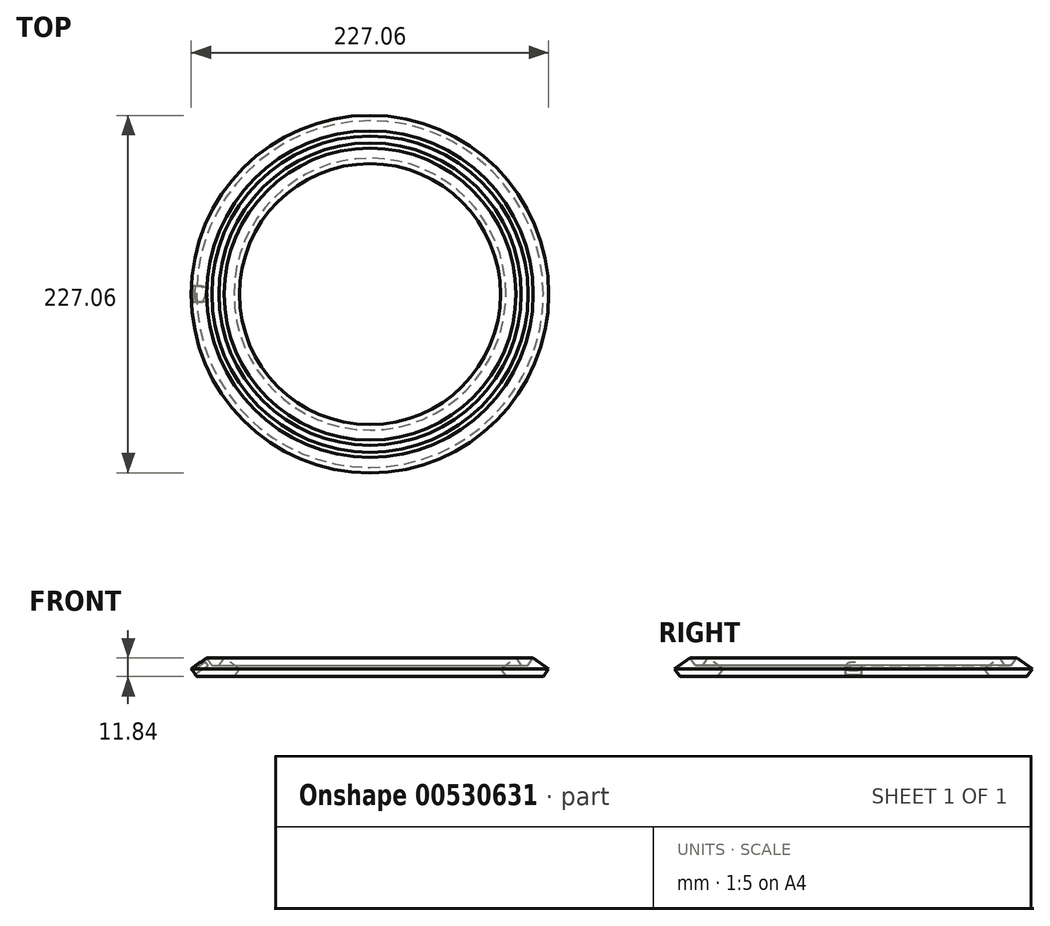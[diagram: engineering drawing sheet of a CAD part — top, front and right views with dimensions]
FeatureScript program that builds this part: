
annotation { "Feature Type Name" : "Feature", "Feature Type Description" : "" }
export const myFeature = defineFeature(function(context is Context, id is Id, definition is map)
    precondition{}
    {
        {
            var Q0;
            Q0=qCreatedBy(makeId("Front.planeOp"),FACE);
            var sketch = newSketch(context, id + "F0", { "sketchPlane" : qUnion([Q0])});
            skLineSegment(sketch, "E0", {"start": v(-110.1, 0) * mm, "end": v(-113.53, 4.92) * mm});
            skLineSegment(sketch, "E1", {"start": v(-113.53, 4.92) * mm, "end": v(-103.68, 11.78) * mm});
            skLineSegment(sketch, "E2", {"start": v(-103.68, 11.78) * mm, "end": v(-100.43, 7.11) * mm});
            skLineSegment(sketch, "E3", {"start": v(-100.43, 7.11) * mm, "end": v(-96.01, 7.11) * mm});
            skLineSegment(sketch, "E4", {"start": v(-96.01, 7.11) * mm, "end": v(-92.67, 11.84) * mm});
            skLineSegment(sketch, "E5", {"start": v(-92.67, 11.84) * mm, "end": v(-82.88, 4.9) * mm});
            skLineSegment(sketch, "E6", {"start": v(-82.88, 4.9) * mm, "end": v(-86.35, 0) * mm});
            skLineSegment(sketch, "E7", {"start": v(-86.35, 0) * mm, "end": v(-110.1, 0) * mm});
            skLineSegment(sketch, "E8", {"start": v(-112.67, 3.7) * mm, "end": v(-104.47, 9.41) * mm});
            skLineSegment(sketch, "E9", {"start": v(-104.47, 9.41) * mm, "end": v(-102.75, 6.95) * mm});
            skLineSegment(sketch, "E10", {"start": v(-102.75, 6.95) * mm, "end": v(-110.96, 1.23) * mm});
            skLineSegment(sketch, "E11", {"start": v(-83.74, 3.67) * mm, "end": v(-91.9, 9.46) * mm});
            skLineSegment(sketch, "E12", {"start": v(-91.9, 9.46) * mm, "end": v(-93.64, 7) * mm});
            skLineSegment(sketch, "E13", {"start": v(-93.64, 7) * mm, "end": v(-85.48, 1.22) * mm});
            skLineSegment(sketch, "E14", {"start": v(-103.61, 8.18) * mm, "end": v(-101.97, 9.32) * mm});
            skLineSegment(sketch, "E15", {"start": v(-92.77, 8.23) * mm, "end": v(-94.4, 9.39) * mm});
            skLineSegment(sketch, "E16", {"start": v(-103.76, 8.4) * mm, "end": v(-102.12, 9.54) * mm});
            skLineSegment(sketch, "E17", {"start": v(-103.46, 7.96) * mm, "end": v(-101.82, 9.1) * mm});
            skLineSegment(sketch, "E18", {"start": v(-92.91, 8.03) * mm, "end": v(-94.55, 9.18) * mm});
            skLineSegment(sketch, "E19", {"start": v(-94.26, 9.6) * mm, "end": v(-92.62, 8.44) * mm});
            skLineSegment(sketch, "E20", {"start": v(-108.57, 6.55) * mm, "end": v(-106.85, 4.09) * mm});
            skLineSegment(sketch, "E21", {"start": v(-87.82, 6.56) * mm, "end": v(-89.56, 4.12) * mm});
            skLineSegment(sketch, "E22", {"start": v(0, 0) * mm, "end": v(0, 20.5) * mm});
            skSolve(sketch);
        }
        {
            var Q0;
            {var subQ1=sQuery(id+"F0.wireOp",EDGE,"E1");Q0=makeQuery(id+"F0.imprint","IMPRINT",FACE,{"disambiguationData":[TD([[makeQuery(id+"F0.imprint","IMPRINT",EDGE,{"derivedFrom":subQ1}),-1.0]])]});}
            var Q1;
            {var subQ5=sQuery(id+"F0.wireOp",EDGE,"E20");Q1=makeQuery(id+"F0.imprint","IMPRINT",FACE,{"disambiguationData":[TD([[makeQuery(id+"F0.imprint","IMPRINT",EDGE,{"derivedFrom":subQ5}),-1.0]])]});}
            var Q2;
            {var subQ4=sQuery(id+"F0.wireOp",EDGE,"E5");Q2=makeQuery(id+"F0.imprint","IMPRINT",FACE,{"disambiguationData":[TD([[makeQuery(id+"F0.imprint","IMPRINT",EDGE,{"derivedFrom":subQ4}),-1.0]])]});}
            var Q3;
            {var subQ11=sQuery(id+"F0.wireOp",EDGE,"E3");Q3=makeQuery(id+"F0.imprint","IMPRINT",FACE,{"disambiguationData":[TD([[makeQuery(id+"F0.imprint","IMPRINT",EDGE,{"derivedFrom":subQ11}),-1.0]])]});}
            var Q4;
            {var subQ0=sQuery(id+"F0.wireOp",EDGE,"E14");Q4=makeQuery(id+"F0.imprint","IMPRINT",FACE,{"disambiguationData":[TD([[makeQuery(id+"F0.imprint","IMPRINT",EDGE,{"derivedFrom":subQ0}),1.0]])]});}
            var Q5;
            {var subQ0=sQuery(id+"F0.wireOp",EDGE,"E14");Q5=makeQuery(id+"F0.imprint","IMPRINT",FACE,{"disambiguationData":[TD([[makeQuery(id+"F0.imprint","IMPRINT",EDGE,{"derivedFrom":subQ0}),-1.0]])]});}
            var Q6;
            {var subQ0=sQuery(id+"F0.wireOp",EDGE,"E15");Q6=makeQuery(id+"F0.imprint","IMPRINT",FACE,{"disambiguationData":[TD([[makeQuery(id+"F0.imprint","IMPRINT",EDGE,{"derivedFrom":subQ0}),1.0]])]});}
            var Q7;
            {var subQ0=sQuery(id+"F0.wireOp",EDGE,"E15");Q7=makeQuery(id+"F0.imprint","IMPRINT",FACE,{"disambiguationData":[TD([[makeQuery(id+"F0.imprint","IMPRINT",EDGE,{"derivedFrom":subQ0}),-1.0]])]});}
            var Q8;
            {var subQ5=sQuery(id+"F0.wireOp",EDGE,"E21");Q8=makeQuery(id+"F0.imprint","IMPRINT",FACE,{"disambiguationData":[TD([[makeQuery(id+"F0.imprint","IMPRINT",EDGE,{"derivedFrom":subQ5}),1.0]])]});}
            var Q9;
            {var subQ6=sQuery(id+"F0.wireOp",EDGE,"E20");Q9=makeQuery(id+"F0.imprint","IMPRINT",FACE,{"disambiguationData":[TD([[makeQuery(id+"F0.imprint","IMPRINT",EDGE,{"derivedFrom":subQ6}),1.0]])]});}
            var Q10;
            {var subQ3=sQuery(id+"F0.wireOp",EDGE,"E21");Q10=makeQuery(id+"F0.imprint","IMPRINT",FACE,{"disambiguationData":[TD([[makeQuery(id+"F0.imprint","IMPRINT",EDGE,{"derivedFrom":subQ3}),-1.0]])]});}
            var Q11;
            Q11=sQuery(id+"F0.wireOp",EDGE,"E22");
            revolve(context, id + "F1", {"entities" : qUnion([Q0, Q1, Q2, Q3, Q4, Q5, Q6, Q7, Q8, Q9, Q10]), "axis" : qUnion([Q11]), "revolveType" : RevolveType.FULL});
        }
        {
            var Q0;
            {var subQ5=sQuery(id+"F0.wireOp",EDGE,"E20");Q0=makeQuery(id+"F0.imprint","IMPRINT",FACE,{"disambiguationData":[TD([[makeQuery(id+"F0.imprint","IMPRINT",EDGE,{"derivedFrom":subQ5}),-1.0]])]});}
            extrude(context, id + "F2", {"entities" : qUnion([Q0]), "operationType" : NewBodyOperationType.REMOVE, "depth" : 5 * mm, "offsetDistance" : 25 * mm, "hasSecondDirection" : true, "secondDirectionOppositeDirection" : true, "secondDirectionDepth" : 5 * mm});
        }
        {
            var Q0;
            {var subQ6=sQuery(id+"F0.wireOp",EDGE,"E20");Q0=makeQuery(id+"F0.imprint","IMPRINT",FACE,{"disambiguationData":[TD([[makeQuery(id+"F0.imprint","IMPRINT",EDGE,{"derivedFrom":subQ6}),1.0]])]});}
            var Q1;
            Q1=sQuery(id+"F0.wireOp",EDGE,"E20");
            revolve(context, id + "F3", {"operationType" : NewBodyOperationType.REMOVE, "entities" : qUnion([Q0]), "axis" : qUnion([Q1]), "revolveType" : RevolveType.FULL});
        }
        {
            var Q0;
            {var subQ5=sQuery(id+"F0.wireOp",EDGE,"E21");Q0=makeQuery(id+"F0.imprint","IMPRINT",FACE,{"disambiguationData":[TD([[makeQuery(id+"F0.imprint","IMPRINT",EDGE,{"derivedFrom":subQ5}),1.0]])]});}
            extrude(context, id + "F4", {"entities" : qUnion([Q0]), "depth" : 5 * mm, "offsetDistance" : 25 * mm, "hasSecondDirection" : true, "secondDirectionOppositeDirection" : true, "secondDirectionDepth" : 5 * mm});
        }
        {
            var Q0;
            {var subQ3=sQuery(id+"F0.wireOp",EDGE,"E21");Q0=makeQuery(id+"F0.imprint","IMPRINT",FACE,{"disambiguationData":[TD([[makeQuery(id+"F0.imprint","IMPRINT",EDGE,{"derivedFrom":subQ3}),-1.0]])]});}
            var Q1;
            Q1=sQuery(id+"F0.wireOp",EDGE,"E21");
            revolve(context, id + "F5", {"operationType" : NewBodyOperationType.ADD, "entities" : qUnion([Q0]), "axis" : qUnion([Q1]), "revolveType" : RevolveType.FULL});
        }
    });
